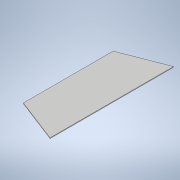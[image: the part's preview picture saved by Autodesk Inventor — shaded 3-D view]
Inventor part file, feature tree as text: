
AUTODESK INVENTOR PART (.ipt)
format: ipt  version: 2021 (Build 250183000, 183)  size: 93,184 bytes
history: native  units: in
note: dims shown in document units (in); Inventor stores cm internally (conversion verified against a paired STEP export)
features: extrude x1, sketch x1
ambient origin geometry x8: Origin, YZ Plane, XZ Plane, XY Plane, X Axis, Y Axis, Z Axis, Center Point
bodies: Solid1 (feature_tree)
feature tree (2):
  extrude  "Extrusion1"  Depth=11.0in
  sketch  "Sketch1"  dims[d0=11.0in d1=11.0in d2=7.76in d3=8.0in d4=8.0in d5=0.125in d6=0.0in]
